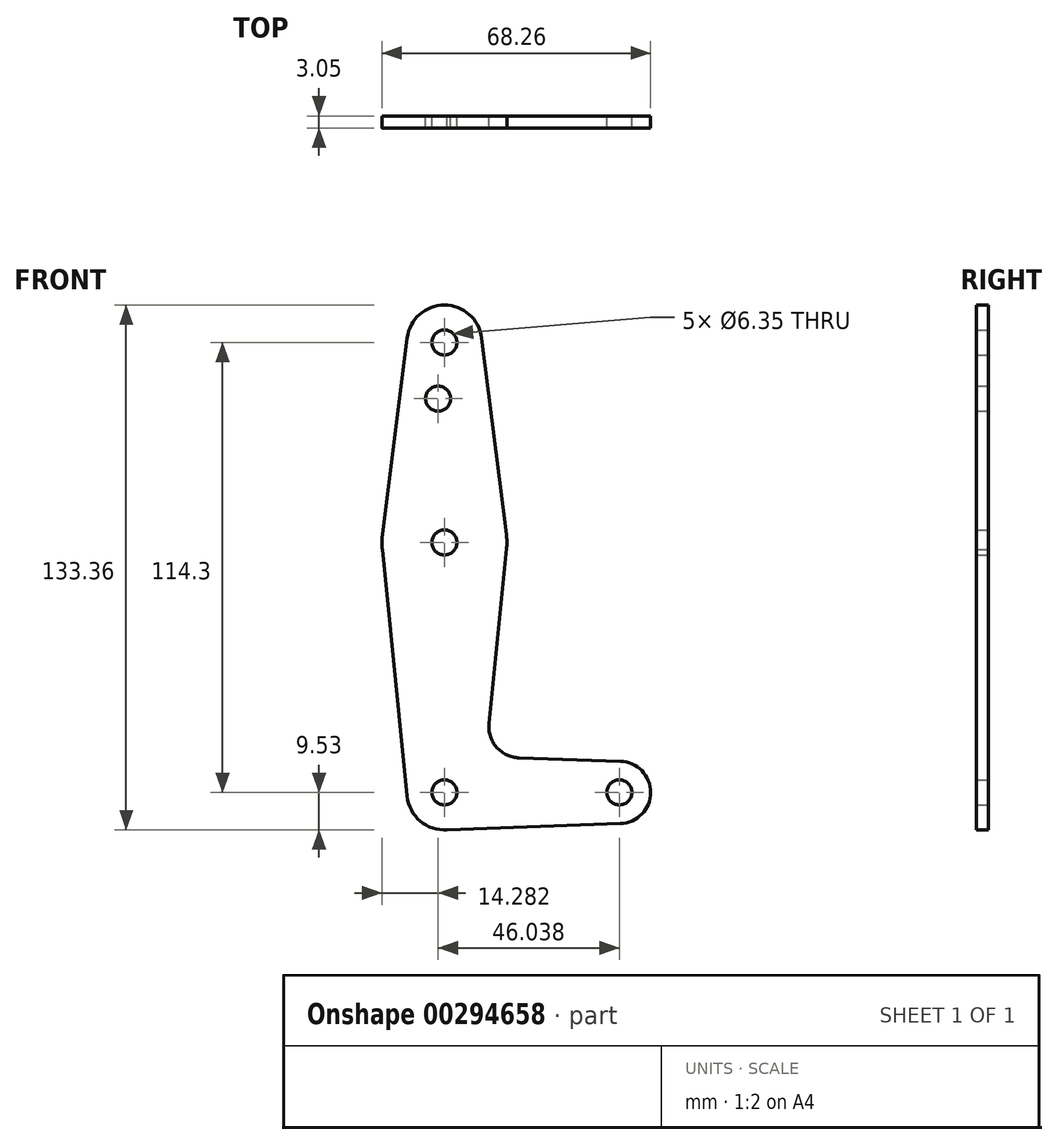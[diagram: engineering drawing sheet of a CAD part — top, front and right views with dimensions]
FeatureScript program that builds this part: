
annotation { "Feature Type Name" : "Feature", "Feature Type Description" : "" }
export const myFeature = defineFeature(function(context is Context, id is Id, definition is map)
    precondition{}
    {
        {
            var Q0;
            Q0=qCreatedBy(makeId("Front.planeOp"),FACE);
            var sketch = newSketch(context, id + "F0", { "sketchPlane" : qUnion([Q0])});
            skCircle(sketch, "E0", {"center": v(0, 0) * mm, "radius": 9.53 * mm});
            skCircle(sketch, "E1", {"center": v(0, 63.5) * mm, "radius": 15.88 * mm});
            skCircle(sketch, "E2", {"center": v(0, 114.3) * mm, "radius": 9.53 * mm});
            skCircle(sketch, "E3", {"center": v(44.45, 0) * mm, "radius": 7.94 * mm});
            skLineSegment(sketch, "E4", {"start": v(0, 63.5) * mm, "end": v(0, 0) * mm, "construction": true});
            skLineSegment(sketch, "E5", {"start": v(0, 114.3) * mm, "end": v(0, 63.5) * mm, "construction": true});
            skLineSegment(sketch, "E6", {"start": v(0, 0) * mm, "end": v(44.45, 0) * mm, "construction": true});
            skLineSegment(sketch, "E7", {"start": v(-9.45, 115.5) * mm, "end": v(-15.75, 65.48) * mm});
            skLineSegment(sketch, "E8", {"start": v(9.45, 115.5) * mm, "end": v(15.75, 65.48) * mm});
            skLineSegment(sketch, "E9", {"start": v(15.8, 61.91) * mm, "end": v(11.33, 17.5) * mm});
            skLineSegment(sketch, "E10", {"start": v(-15.78, 61.75) * mm, "end": v(-9.48, -0.95) * mm});
            skLineSegment(sketch, "E11", {"start": v(18.99, 8.76) * mm, "end": v(44.7, 7.93) * mm});
            skLineSegment(sketch, "E12", {"start": v(0, -9.53) * mm, "end": v(44.73, -7.93) * mm});
            skCircle(sketch, "E13", {"center": v(0, 114.3) * mm, "radius": 3.18 * mm});
            skCircle(sketch, "E14", {"center": v(0, 63.5) * mm, "radius": 3.18 * mm});
            skCircle(sketch, "E15", {"center": v(0, 0) * mm, "radius": 3.18 * mm});
            skCircle(sketch, "E16", {"center": v(44.45, 0) * mm, "radius": 3.18 * mm});
            skCircle(sketch, "E17", {"center": v(-1.59, 100.03) * mm, "radius": 3.18 * mm});
            skArc(sketch, "E18.filletArc", {"start": v(11.33, 17.5) * mm, "mid": v(13.26, 11.47) * mm, "end": v(18.99, 8.76) * mm});
            skSolve(sketch);
        }
        {
            var Q0;
            Q0 = qSketchRegion(id + "F0", true);
            extrude(context, id + "F1", {"entities" : qUnion([Q0]), "depth" : 3.05 * mm});
        }
    });
